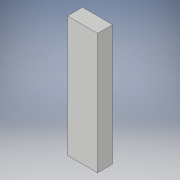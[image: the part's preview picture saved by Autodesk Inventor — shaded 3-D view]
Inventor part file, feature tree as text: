
AUTODESK INVENTOR PART (.ipt)
format: ipt  version: 2017 (Build 210142000, 142)  size: 89,088 bytes
history: native  units: in
note: dims shown in document units (in); Inventor stores cm internally (conversion verified against a paired STEP export)
features: extrude x1, sketch x1
ambient origin geometry x8: Origin, YZ Plane, XZ Plane, XY Plane, X Axis, Y Axis, Z Axis, Center Point
bodies: Solid1 (feature_tree)
feature tree (2):
  extrude  "Extrusion1"  Depth=0.75in
  sketch  "Sketch1"  dims[d0=1.5in d1=0.75in d2=6.0in d3=0.0in]
